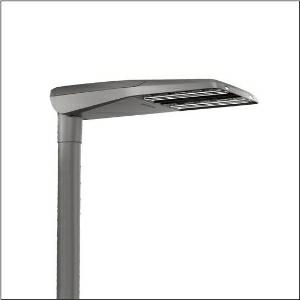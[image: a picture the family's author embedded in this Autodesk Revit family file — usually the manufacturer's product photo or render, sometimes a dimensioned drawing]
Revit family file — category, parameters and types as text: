
# Revit family: streetlight_sl_11_iq_midi___st1_2p1_0_5xc3g51f08me_c537
name_source: partatom
category: Lighting Fixtures
units: mm (PartAtom-declared; Revit-internal decimal feet)

## family parameters
Cut with Voids When Loaded = No
Host = Face
Light Source = No
Part Type = Normal
Room Calculation Point = No
Round Connector Dimension = Use Diameter
Shared = No

## types (1)
- --- (1 x LED, 17750 lm, 121.7 W, 3000K)
    Apparent Load = 122 VA
    CIE Flux Codes = 31 68 95 100 100
    Color Rendering = 70
    Color Temperature = 3000K
    Default Elevation = 1800 mm
    Description = Streetlight SL 11 iQ midi, mast luminaire, primary light control with 3 zone facetted reflector, of plastic, silver coated, highly specular, primary optical cover: cover, of PMMA, transparent, light distribution: ST1.2P1.0, light emission: direct distribution, primary light characteristic: asymmetric, installation type: post-top, side-entry, lamps: LED, High Power LED, rated values: 17.750lm | 121,7W | 145,9lm/W (begin service life); end service life: 17.750lm | 129W; at 50% lumin. flux: 8.875lm | 56W | 158,5lm/W, colour temperature: 3000K, colour rendering: CRI > 70, light colour: 730, light setting 1 begin service life: 100% | 17.750lm | 121,7W | 145,9lm/W | 3.000K, light setting 1 end service life: 129W, further light settings possible, control: Street-Remote, optimised constant luminous flux control (CLO 2.0), Auto-Match, Desk-Remote (wireless, voltage-free reading and setting of iQ features in the workshop via application-optimized NFC function/RFID function), Light-Fading, Smart-Wire, Night-Set, Lumen-Switch, Temp-Guard, with cable H07RN-F 3x 1.5mm², mains connection: 230..240V, AC, 50/60Hz, connection cable pre-assembled, cable length: 12,5m, luminaire housing, of diecast aluminium, powder-coated, SITECO metallic grey (DB 702S), please order mast flange separately, inclination adjustable without tools: 0°, 5°, 10°, 15° (post-top) | 0°, -5°, -10°, -15° (side-entry), sealing non-destructively replaceable, multi-level sealing system, length: 780mm, width: 376mm, height: 118mm, mast flange for spigot size: 42mm (side-entry): 5XC10008XM4, 60/48mm (side-entry/post-top): 5XC10108XM2, 76/60mm (side-entry/post-top): 5XC10108XM1, equipment: Power, protection rating (complete): IP66, insulation class (complete): insulation class II (safety insulation), certification: CE, ENEC, ENEC+, VDE, impact resistance: IK10, permissible operating ambient temperature for outdoor applications: -25..+50°C, standard-compliant lighting for roads and squares, Environmental Product Declaration (EPD) tested and certified by an independent institute, packaging unit: 1 piece

Light Distribution: ST1.2P1.0
    Height = 118 mm
    Lamp = 1 x LED
    Lamp Light Flux = 17750 lm
    Lamp Power = 121.7 W
    Lamp count = 1
    Length = 780 mm
    Luminous efficacy = 146 lm/W
    Manufacturer = Siteco
    ModVariant = No
    Model = 5XC3G51F08ME
    Number of Poles = 1
    OnlyDefault = Yes
    Power Factor = 1
    Product Name = Streetlight SL 11 iQ midi | ST1.2P1.0
    Product group = mast luminaire | pylon top
    ProductGroupID = 6100
    Protection Class = Protection class II
    Protection Degree = IP 66
    RLX_Detail_Level = 1
    RLX_Emergency_Light_Flux = 0 lm
    RLX_Emergency_Type = 0
    RLX_Emergency_Type_DB = No
    RlxData = <blob elided: 70893 chars, md5=552bee7b>
    Socket = socket
    Standby Power = 0 W
    System Light Flux = 17750 lm
    System Power = 122 W
    Type Comments = factory setting: luminous flux: 100 % | dim-lin: 254 | 544 mA
    Type Image = l_1005960.jpg
    URL = http://relux.com
    VarID = @adj_044131
    Voltage = 0 V
    Weight = 0.00 kg
    Width = 376 mm

## geometry (parser evidence)
native form markers: Blend x4, Sweep x8
no freeform markers — native parametric forms only
